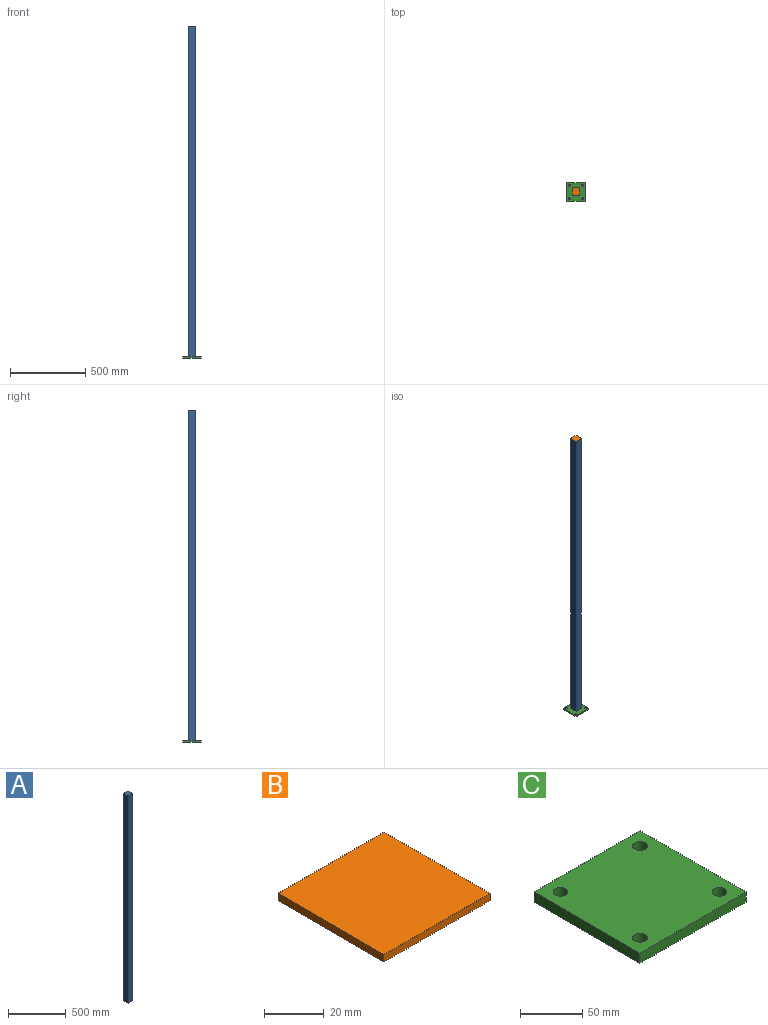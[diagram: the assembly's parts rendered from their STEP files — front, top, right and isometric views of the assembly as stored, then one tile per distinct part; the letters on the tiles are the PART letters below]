
ASSEMBLY  parts=3 mates=2
PART A: 6 faces, bbox 50x50x2200 mm
  f0: plane 2200x50mm, normal (1,0,0), area 110000mm2, adj f1,f3,f4,f5
  f1: plane 2200x50mm, normal (0,1,0), area 110000mm2, adj f0,f2,f4,f5
  f2: plane 2200x50mm, normal (-1,0,0), area 110000mm2, adj f1,f3,f4,f5
  f3: plane 2200x50mm, normal (0,-1,0), area 110000mm2, adj f0,f2,f4,f5
  f4: plane 50x50mm, normal (0,0,1), area 2500mm2, adj f0,f1,f2,f3
  f5: plane 50x50mm, normal (0,0,-1), area 2500mm2, adj f0,f1,f2,f3
PART B: 6 faces, bbox 50x50x3 mm
  f0: plane 50x3mm, normal (0,1,0), area 150mm2, adj f1,f3,f4,f5
  f1: plane 50x3mm, normal (-1,0,0), area 150mm2, adj f0,f2,f4,f5
  f2: plane 50x3mm, normal (0,-1,0), area 150mm2, adj f1,f3,f4,f5
  f3: plane 50x3mm, normal (1,0,0), area 150mm2, adj f0,f2,f4,f5
  f4: plane 50x50mm, normal (0,0,1), area 2500mm2, adj f0,f1,f2,f3
  f5: plane 50x50mm, normal (0,0,-1), area 2500mm2, adj f0,f1,f2,f3
PART C: 10 faces, bbox 120x120x10 mm
  f0: plane 120x10mm, normal (0,1,0), area 1200mm2, adj f1,f3,f4,f5
  f1: plane 120x10mm, normal (-1,0,0), area 1200mm2, adj f0,f2,f4,f5
  f2: plane 120x10mm, normal (0,-1,0), area 1200mm2, adj f1,f3,f4,f5
  f3: plane 120x10mm, normal (1,0,0), area 1200mm2, adj f0,f2,f4,f5
  f4: plane 120x120mm, normal (0,0,1), area 13947.6mm2, adj f0,f1,f2,f3,f6,f7,f8,f9
  f5: plane 120x120mm, normal (0,0,-1), area 13947.6mm2, adj f0,f1,f2,f3,f6,f7,f8,f9
  f6: cylinder r=6mm len=12mm, axis (0,0,1), area 377mm2, adj f4,f5
  f7: cylinder r=6mm len=12mm, axis (0,0,1), area 377mm2, adj f4,f5
  f8: cylinder r=6mm len=12mm, axis (0,0,1), area 377mm2, adj f4,f5
  f9: cylinder r=6mm len=12mm, axis (0,0,1), area 377mm2, adj f4,f5
PLACE A t=(75.46,65.39,-63.63)mm
PLACE B t=(75.46,65.39,2136.37)mm
PLACE C t=(75.46,65.39,-73.63)mm
MATE fastened B.f5 <-> A.f4  axis (0,0,-1) through (75.46,65.39,2136.37)mm
MATE fastened A.f5 <-> C.f4  axis (0,0,-1) through (75.46,65.39,-63.63)mm
